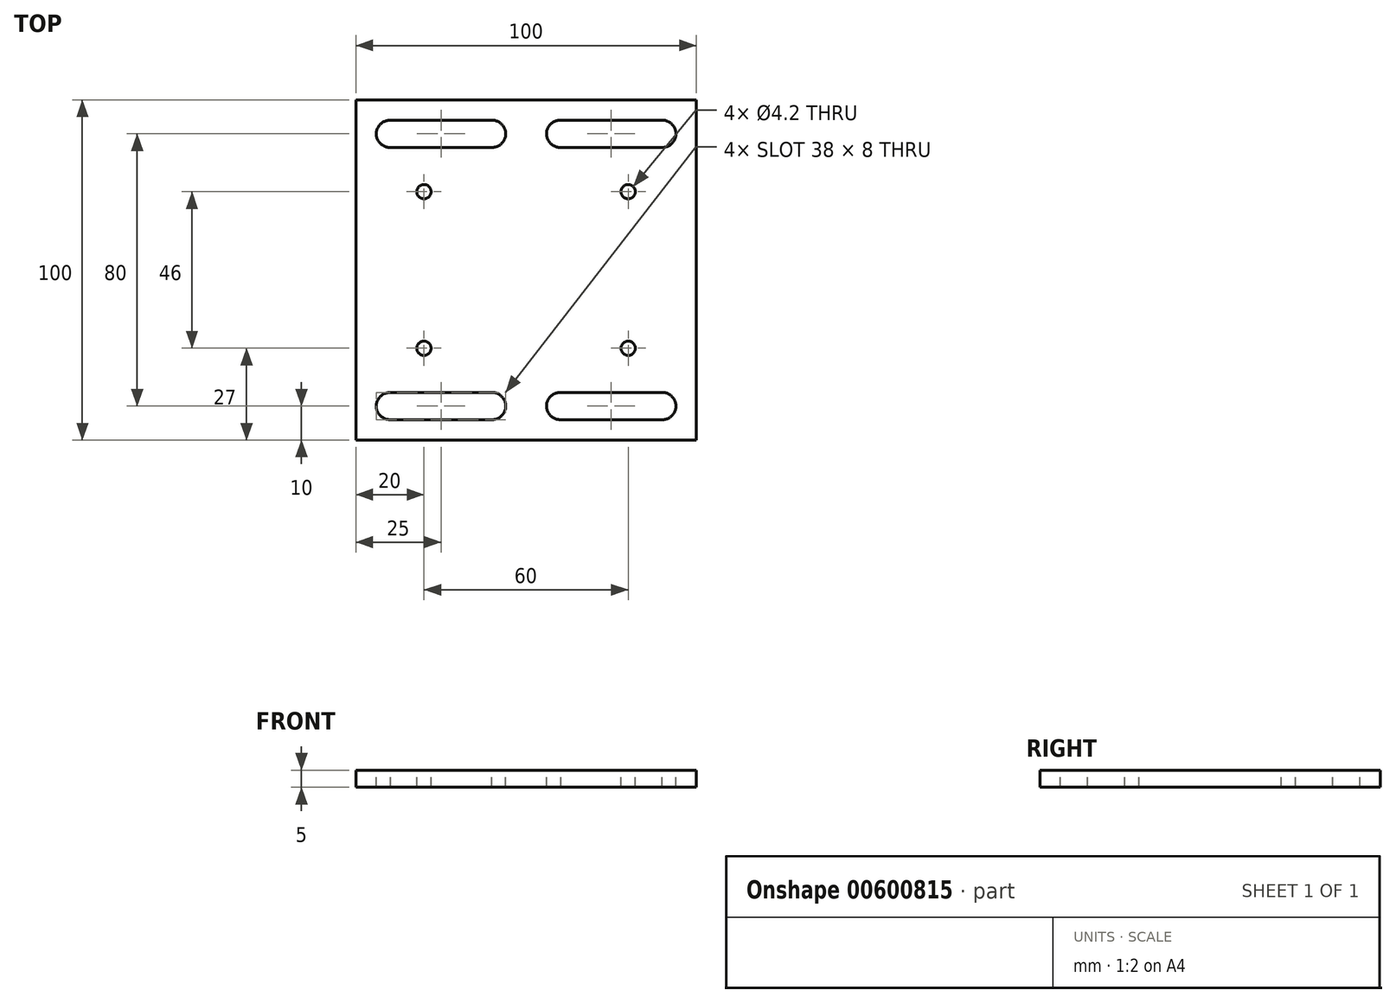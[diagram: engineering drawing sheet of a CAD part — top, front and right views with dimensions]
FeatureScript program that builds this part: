
annotation { "Feature Type Name" : "Feature", "Feature Type Description" : "" }
export const myFeature = defineFeature(function(context is Context, id is Id, definition is map)
    precondition{}
    {
        {
            var Q0;
            Q0=qCreatedBy(makeId("Top.planeOp"),FACE);
            var sketch = newSketch(context, id + "F0", { "sketchPlane" : qUnion([Q0])});
            skLineSegment(sketch, "E0.bottom", {"start": v(0, 0) * mm, "end": v(100, 0) * mm});
            skLineSegment(sketch, "E0.top", {"start": v(0, 100) * mm, "end": v(100, 100) * mm});
            skLineSegment(sketch, "E0.left", {"start": v(0, 0) * mm, "end": v(0, 100) * mm});
            skLineSegment(sketch, "E0.right", {"start": v(100, 0) * mm, "end": v(100, 100) * mm});
            skSolve(sketch);
        }
        {
            var Q0;
            Q0=makeQuery(id+"F0.imprint","IMPRINT",FACE,{"disambiguationData":[TD([[makeQuery(id+"F0.imprint","IMPRINT",EDGE,{"derivedFrom":sQuery(id+"F0.wireOp",EDGE,"E0.bottom")}),1.0]])]});
            extrude(context, id + "F1", {"entities" : qUnion([Q0]), "depth" : 5 * mm, "offsetDistance" : 25 * mm});
        }
        {
            var Q0;
            Q0=makeQuery(id+"F1.opExtrude","CAP_FACE",FACE,{"disambiguationData":[OSD([sQuery(id+"F0.wireOp",EDGE,"E0.bottom"),sQuery(id+"F0.wireOp",EDGE,"E0.top"),sQuery(id+"F0.wireOp",EDGE,"E0.left"),sQuery(id+"F0.wireOp",EDGE,"E0.right")])],"isStart":false});
            var sketch = newSketch(context, id + "F2", { "sketchPlane" : qUnion([Q0])});
            skArc(sketch, "E1", {"start": v(10.19, 14) * mm, "mid": v(6, 10.1) * mm, "end": v(10, 6) * mm});
            skArc(sketch, "E2", {"start": v(39.94, 6) * mm, "mid": v(44, 9.97) * mm, "end": v(40, 14) * mm});
            skLineSegment(sketch, "E3", {"start": v(9.8, 14) * mm, "end": v(40, 14) * mm});
            skLineSegment(sketch, "E4", {"start": v(39.94, 6) * mm, "end": v(10, 6) * mm});
            skArc(sketch, "E5.0.1.0", {"start": v(39.94, 86) * mm, "mid": v(44, 89.97) * mm, "end": v(40, 94) * mm});
            skLineSegment(sketch, "E5.0.1.1", {"start": v(9.8, 94) * mm, "end": v(40, 94) * mm});
            skArc(sketch, "E5.0.1.2", {"start": v(10.19, 94) * mm, "mid": v(6, 90.1) * mm, "end": v(10, 86) * mm});
            skLineSegment(sketch, "E5.0.1.3", {"start": v(39.94, 86) * mm, "end": v(10, 86) * mm});
            skArc(sketch, "E5.1.0.0", {"start": v(89.94, 6) * mm, "mid": v(94, 9.97) * mm, "end": v(90, 14) * mm});
            skLineSegment(sketch, "E5.1.0.1", {"start": v(59.8, 14) * mm, "end": v(90, 14) * mm});
            skArc(sketch, "E5.1.0.2", {"start": v(60.19, 14) * mm, "mid": v(56, 10.1) * mm, "end": v(60, 6) * mm});
            skLineSegment(sketch, "E5.1.0.3", {"start": v(89.94, 6) * mm, "end": v(60, 6) * mm});
            skArc(sketch, "E5.1.1.0", {"start": v(89.94, 86) * mm, "mid": v(94, 89.97) * mm, "end": v(90, 94) * mm});
            skLineSegment(sketch, "E5.1.1.1", {"start": v(59.8, 94) * mm, "end": v(90, 94) * mm});
            skArc(sketch, "E5.1.1.2", {"start": v(60.19, 94) * mm, "mid": v(56, 90.1) * mm, "end": v(60, 86) * mm});
            skLineSegment(sketch, "E5.1.1.3", {"start": v(89.94, 86) * mm, "end": v(60, 86) * mm});
            skLineSegment(sketch, "E5.direction1", {"start": v(10, 6) * mm, "end": v(60, 6) * mm, "construction": true});
            skLineSegment(sketch, "E5.direction2", {"start": v(10, 6) * mm, "end": v(10, 86) * mm, "construction": true});
            skSolve(sketch);
        }
        {
            var Q0;
            Q0 = qSketchRegion(id + "F2", true);
            extrude(context, id + "F3", {"entities" : qUnion([Q0]), "operationType" : NewBodyOperationType.REMOVE, "oppositeDirection" : true, "depth" : 25 * mm, "offsetDistance" : 25 * mm});
        }
        {
            var Q0;
            Q0=makeQuery(id+"F1.opExtrude","CAP_FACE",FACE,{"disambiguationData":[OSD([sQuery(id+"F0.wireOp",EDGE,"E0.bottom"),sQuery(id+"F0.wireOp",EDGE,"E0.top"),sQuery(id+"F0.wireOp",EDGE,"E0.left"),sQuery(id+"F0.wireOp",EDGE,"E0.right")])],"isStart":false});
            var sketch = newSketch(context, id + "F4", { "sketchPlane" : qUnion([Q0])});
            skLineSegment(sketch, "E6", {"start": v(0, 50) * mm, "end": v(100, 50) * mm, "construction": true});
            skCircle(sketch, "E7", {"center": v(20, 73) * mm, "radius": 2.1 * mm});
            skCircle(sketch, "E8", {"center": v(20, 27) * mm, "radius": 2.1 * mm});
            skCircle(sketch, "E9.1.0.0", {"center": v(80, 27) * mm, "radius": 2.1 * mm});
            skCircle(sketch, "E9.1.0.1", {"center": v(80, 73) * mm, "radius": 2.1 * mm});
            skLineSegment(sketch, "E9.direction1", {"start": v(20, 27) * mm, "end": v(80, 27) * mm, "construction": true});
            skSolve(sketch);
        }
        {
            var Q0;
            Q0 = qSketchRegion(id + "F4", true);
            extrude(context, id + "F5", {"entities" : qUnion([Q0]), "operationType" : NewBodyOperationType.REMOVE, "oppositeDirection" : true, "depth" : 25 * mm, "offsetDistance" : 25 * mm});
        }
    });
